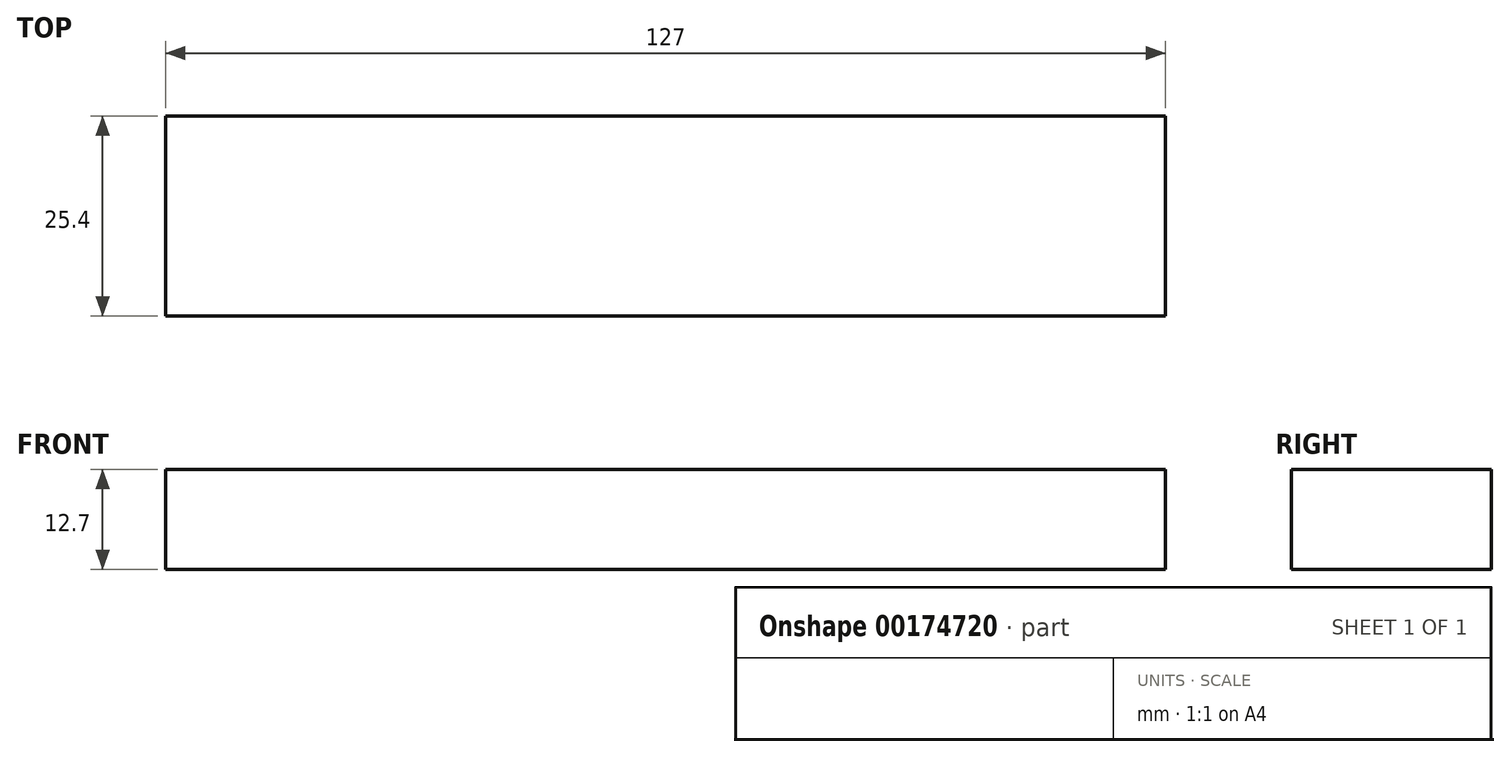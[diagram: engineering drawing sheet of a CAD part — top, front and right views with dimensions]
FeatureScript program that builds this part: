
annotation { "Feature Type Name" : "Feature", "Feature Type Description" : "" }
export const myFeature = defineFeature(function(context is Context, id is Id, definition is map)
    precondition{}
    {
        {
            var Q0;
            Q0=qCreatedBy(makeId("Front.planeOp"),FACE);
            var sketch = newSketch(context, id + "F0", { "sketchPlane" : qUnion([Q0])});
            skLineSegment(sketch, "E0.bottom", {"start": v(-50.8, 38.1) * mm, "end": v(76.2, 38.1) * mm});
            skLineSegment(sketch, "E0.top", {"start": v(-50.8, 25.4) * mm, "end": v(76.2, 25.4) * mm});
            skLineSegment(sketch, "E0.left", {"start": v(-50.8, 38.1) * mm, "end": v(-50.8, 25.4) * mm});
            skLineSegment(sketch, "E0.right", {"start": v(76.2, 38.1) * mm, "end": v(76.2, 25.4) * mm});
            skSolve(sketch);
        }
        {
            var Q0;
            Q0 = qSketchRegion(id + "F0", true);
            extrude(context, id + "F1", {"entities" : qUnion([Q0]), "endBound" : BoundingType.SYMMETRIC, "depth" : 25.4 * mm});
        }
    });
